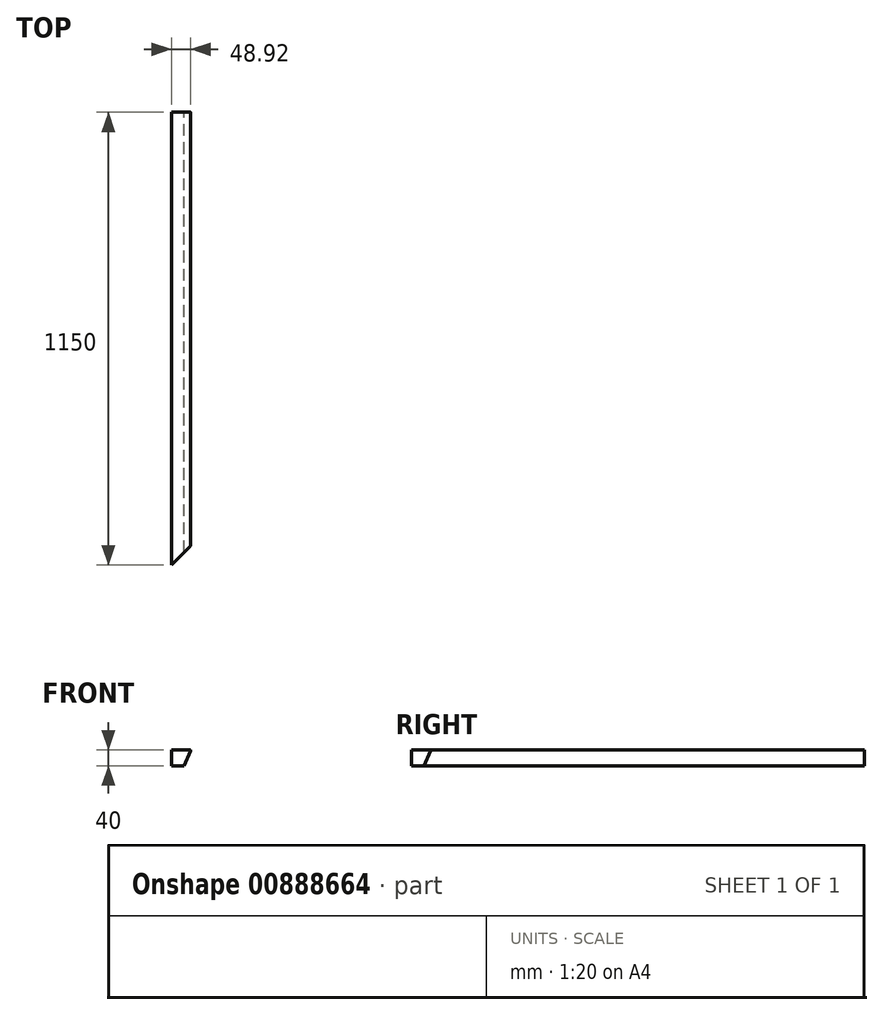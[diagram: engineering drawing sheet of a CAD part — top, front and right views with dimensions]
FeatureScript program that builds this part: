
annotation { "Feature Type Name" : "Feature", "Feature Type Description" : "" }
export const myFeature = defineFeature(function(context is Context, id is Id, definition is map)
    precondition{}
    {
        {
            var Q0;
            Q0=qCreatedBy(makeId("Front.planeOp"),FACE);
            var sketch = newSketch(context, id + "F0", { "sketchPlane" : qUnion([Q0])});
            skLineSegment(sketch, "E0.bottom", {"start": v(0, 0) * mm, "end": v(32.2, 0) * mm});
            skLineSegment(sketch, "E0.top", {"start": v(0, 40) * mm, "end": v(50, 40) * mm});
            skLineSegment(sketch, "E0.left", {"start": v(0, 0) * mm, "end": v(0, 40) * mm});
            skLineSegment(sketch, "E1", {"start": v(50, 40) * mm, "end": v(32.2, 0) * mm});
            skSolve(sketch);
        }
        {
            var Q0;
            Q0 = qSketchRegion(id + "F0", true);
            extrude(context, id + "F1", {"entities" : qUnion([Q0]), "depth" : 1150 * mm, "offsetDistance" : 25 * mm});
        }
        {
            var Q0;
            Q0=makeQuery(id+"F1.opExtrude","SWEPT_EDGE",EDGE,{"disambiguationData":[OSD([sQuery(id+"F0.wireOp",EDGE,"E0.top"),sQuery(id+"F0.wireOp",EDGE,"E1")])]});
            fillet(context, id + "F2", {"entities" : qUnion([Q0]), "radius" : 2 * mm, "tangentPropagation" : true, "allowEdgeOverflow" : false});
        }
        {
            var Q0;
            Q0=makeQuery(id+"F1.opExtrude","SWEPT_FACE",FACE,{"disambiguationData":[OSD([sQuery(id+"F0.wireOp",EDGE,"E0.top")])]});
            var sketch = newSketch(context, id + "F3", { "sketchPlane" : qUnion([Q0])});
            skLineSegment(sketch, "E2", {"start": v(0, -1150) * mm, "end": v(74.08, -1075.92) * mm});
            skLineSegment(sketch, "E3", {"start": v(0, -1150) * mm, "end": v(53.24, -1150) * mm});
            skLineSegment(sketch, "E4", {"start": v(53.24, -1150) * mm, "end": v(53.24, -1096.76) * mm});
            skSolve(sketch);
        }
        {
            var Q0;
            {var subQ0=sQuery(id+"F3.wireOp",EDGE,"E3");var subQ1=sQuery(id+"F3.wireOp",EDGE,"E2");var subQ2=sQuery(id+"F0.wireOp",EDGE,"E0.top");var subQ3=makeQuery(id+"F3.imprint","INTERSECT",VERTEX,{"derivedFrom":[makeQuery(id+"F1.opExtrude","SWEPT_EDGE",EDGE,{"disambiguationData":[OSD([subQ2,sQuery(id+"F0.wireOp",EDGE,"E0.left")])]}),subQ1,subQ0]});Q0=makeQuery(id+"F3.imprint","IMPRINT",FACE,{"disambiguationData":[TD([[makeQuery(id+"F3.imprint","IMPRINT",EDGE,{"disambiguationData":[TD([[subQ3,-1.0]])],"derivedFrom":subQ1}),-1.0]])]});}
            var Q1;
            {var subQ0=sQuery(id+"F3.wireOp",EDGE,"E4");Q1=makeQuery(id+"F3.imprint","IMPRINT",FACE,{"disambiguationData":[TD([[makeQuery(id+"F3.imprint","IMPRINT",EDGE,{"derivedFrom":subQ0}),1.0]])]});}
            extrude(context, id + "F4", {"entities" : qUnion([Q0, Q1]), "operationType" : NewBodyOperationType.REMOVE, "endBound" : BoundingType.THROUGH_ALL, "oppositeDirection" : true, "depth" : 25 * mm, "offsetDistance" : 25 * mm});
        }
    });
